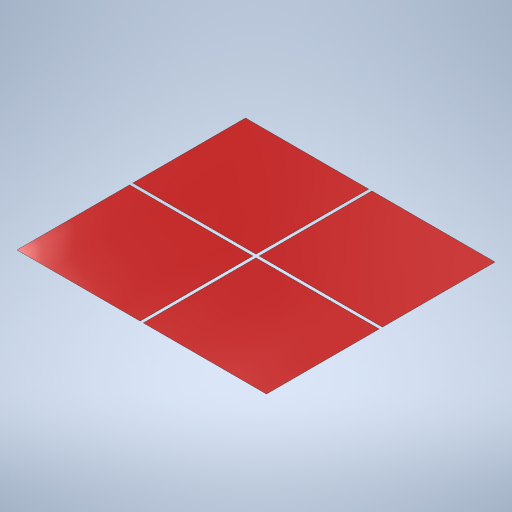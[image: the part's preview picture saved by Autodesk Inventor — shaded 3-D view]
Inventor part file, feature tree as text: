
AUTODESK INVENTOR PART (.ipt)
format: ipt  version: 2023 (Build 270158000, 158)  size: 252,928 bytes
history: native  units: in
note: dims shown in document units (in); Inventor stores cm internally (conversion verified against a paired STEP export)
features: extrude x2, sketch x2
ambient origin geometry x8: Origin, YZ Plane, XZ Plane, XY Plane, X Axis, Y Axis, Z Axis, Center Point
bodies: Solid1 (feature_tree)
feature tree (4):
  extrude  "Extrusion1"  Depth=1.7165in
  extrude  "Extrusion2"  Depth=0.0236in
  sketch  "Sketch1"  dims[d0=1.874in d1=1.7165in]
  sketch  "Sketch2"  dims[d2=0.0004in d3=0.0in d4=0.0236in d6=0.0004in d7=0.0in d8=0.0236in]
